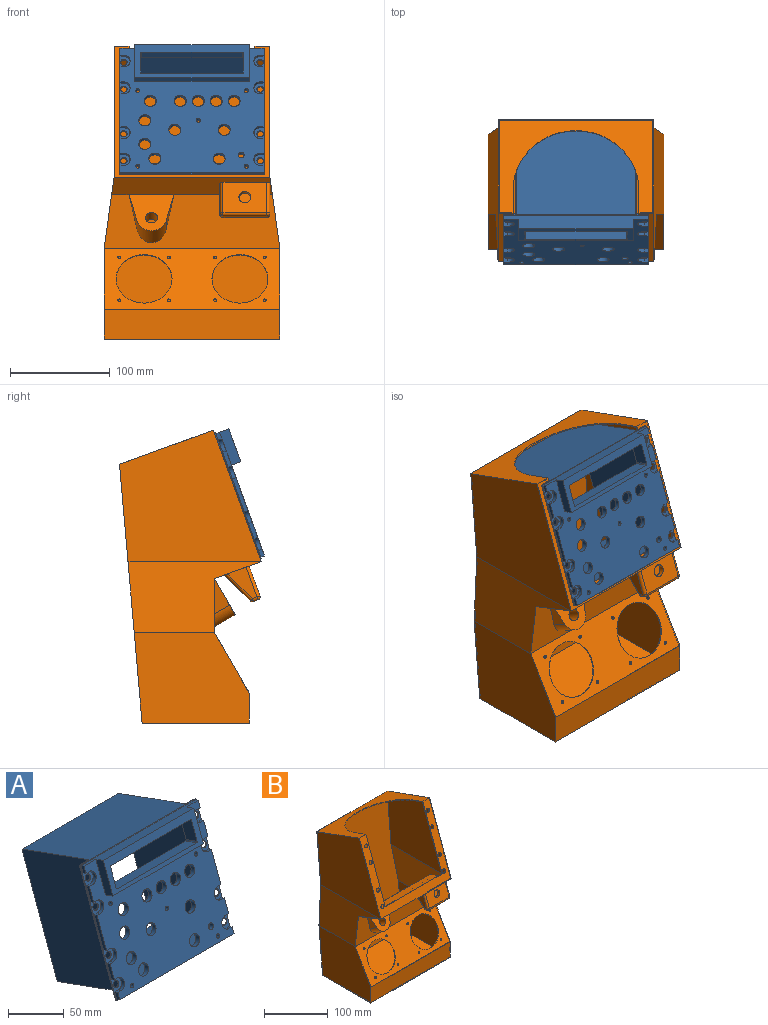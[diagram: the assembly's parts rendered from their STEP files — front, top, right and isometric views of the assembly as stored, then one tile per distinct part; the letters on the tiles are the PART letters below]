
ASSEMBLY  parts=2 mates=3
PART A: 89 faces, bbox 146x134.6x157.7 mm
  f0: plane 144.4x123.81mm, normal (0,-0.94,0.34), area 12776.2mm2, adj f8,f9,f10,f11,f12,f13,f14,f15
  f1: plane 120.61x120mm, normal (0,0.94,-0.34), area 11712.5mm2, adj f54,f55,f56,f57,f60,f61,f62,f63
  f2: plane 146x125.31mm, normal (0,0.94,-0.34), area 3302.6mm2, adj f4,f5,f6,f7,f44,f45,f46,f47
  f3: plane 146x125.31mm, normal (0,-0.94,0.34), area 1089.9mm2, adj f4,f5,f6,f7,f8,f9,f10,f11
  f4: plane 146x85.51mm, normal (0,0.34,0.94), area 11126mm2, adj f2,f3,f5,f7,f52,f53,f59
  f5: plane 125.65x46.55mm, normal (-1,0,0), area 133.4mm2, adj f2,f3,f4,f6
  f6: plane 146x0.94mm, normal (0,-0.34,-0.94), area 146mm2, adj f2,f3,f5,f7
  f7: plane 125.65x46.55mm, normal (1,0,0), area 133.4mm2, adj f2,f3,f4,f6
  f8: plane 8.08x6.2mm, normal (-1,0,0), area 28.6mm2, adj f0,f3,f9,f43
  f9: plane 144.4x3.76mm, normal (0,-0.34,-0.94), area 577.6mm2, adj f0,f3,f8,f10
  f10: plane 8.08x6.2mm, normal (1,0,0), area 28.6mm2, adj f0,f3,f9,f11
  f11: plane 3.96x3.76mm, normal (0,0.34,0.94), area 15.9mm2, adj f0,f3,f10,f12
  f12: cylinder r=6.35mm len=13.3mm, axis (0,0.94,-0.34), area 79.8mm2, adj f0,f3,f11,f13
  f13: plane 3.96x3.76mm, normal (0,-0.34,-0.94), area 15.9mm2, adj f0,f3,f12,f14
  f14: plane 16.29x9.19mm, normal (1,0,0), area 63.5mm2, adj f0,f3,f13,f15
  f15: plane 3.96x3.76mm, normal (0,0.34,0.94), area 15.9mm2, adj f0,f3,f14,f16
  f16: cylinder r=6.35mm len=13.3mm, axis (0,0.94,-0.34), area 79.8mm2, adj f0,f3,f15,f17
  f17: plane 3.96x3.76mm, normal (0,-0.34,-0.94), area 15.9mm2, adj f0,f3,f16,f18
  f18: plane 34.19x15.7mm, normal (1,0,0), area 139.7mm2, adj f0,f3,f17,f19
  f19: plane 3.96x3.76mm, normal (0,0.34,0.94), area 15.9mm2, adj f0,f3,f18,f20
  f20: cylinder r=6.35mm len=13.3mm, axis (0,0.94,-0.34), area 79.8mm2, adj f0,f3,f19,f21
  f21: plane 3.96x3.76mm, normal (0,-0.34,-0.94), area 15.9mm2, adj f0,f3,f20,f22
  f22: plane 16.29x9.19mm, normal (1,0,0), area 63.5mm2, adj f0,f3,f21,f23
  f23: plane 3.96x3.76mm, normal (0,0.34,0.94), area 15.9mm2, adj f0,f3,f22,f24
  f24: cylinder r=6.35mm len=13.3mm, axis (0,0.94,-0.34), area 79.8mm2, adj f0,f3,f23,f25
  f25: plane 3.96x3.76mm, normal (0,-0.34,-0.94), area 15.9mm2, adj f0,f3,f24,f26
  f26: plane 8.08x6.2mm, normal (1,0,0), area 28.6mm2, adj f0,f3,f25,f27
  f27: plane 144.4x13.16mm, normal (0,0.34,0.94), area 1721.6mm2, adj f0,f3,f26,f28,f77,f78,f80
  f28: plane 8.08x6.2mm, normal (-1,0,0), area 28.6mm2, adj f0,f3,f27,f29
  f29: plane 3.96x3.76mm, normal (0,-0.34,-0.94), area 15.9mm2, adj f0,f3,f28,f30
  f30: cylinder r=6.35mm len=13.3mm, axis (0,0.94,-0.34), area 79.8mm2, adj f0,f3,f29,f31
  f31: plane 3.96x3.76mm, normal (0,0.34,0.94), area 15.9mm2, adj f0,f3,f30,f32
  f32: plane 16.29x9.19mm, normal (-1,0,0), area 63.5mm2, adj f0,f3,f31,f33
  f33: plane 3.96x3.76mm, normal (0,-0.34,-0.94), area 15.9mm2, adj f0,f3,f32,f34
  f34: cylinder r=6.35mm len=13.3mm, axis (0,0.94,-0.34), area 79.8mm2, adj f0,f3,f33,f35
  f35: plane 3.96x3.76mm, normal (0,0.34,0.94), area 15.9mm2, adj f0,f3,f34,f36
  f36: plane 34.19x15.7mm, normal (-1,0,0), area 139.7mm2, adj f0,f3,f35,f37
  f37: plane 3.96x3.76mm, normal (0,-0.34,-0.94), area 15.9mm2, adj f0,f3,f36,f38
  f38: cylinder r=6.35mm len=13.3mm, axis (0,0.94,-0.34), area 79.8mm2, adj f0,f3,f37,f39
  f39: plane 3.96x3.76mm, normal (0,0.34,0.94), area 15.9mm2, adj f0,f3,f38,f40
  f40: plane 16.29x9.19mm, normal (-1,0,0), area 63.5mm2, adj f0,f3,f39,f41
  f41: plane 3.96x3.76mm, normal (0,-0.34,-0.94), area 15.9mm2, adj f0,f3,f40,f42
  f42: cylinder r=6.35mm len=13.3mm, axis (0,0.94,-0.34), area 79.8mm2, adj f0,f3,f41,f43
  f43: plane 3.96x3.76mm, normal (0,0.34,0.94), area 15.9mm2, adj f0,f3,f8,f42
  f44: cylinder r=3.24mm len=6.48mm, axis (0,-0.94,0.34), area 20.4mm2, adj f2,f3
  f45: cylinder r=3.24mm len=6.48mm, axis (0,-0.94,0.34), area 20.4mm2, adj f2,f3
  f46: cylinder r=3.24mm len=6.48mm, axis (0,-0.94,0.34), area 20.4mm2, adj f2,f3
  f47: cylinder r=3.24mm len=6.48mm, axis (0,-0.94,0.34), area 20.4mm2, adj f2,f3
  f48: cylinder r=3.24mm len=6.48mm, axis (0,-0.94,0.34), area 20.4mm2, adj f2,f3
  f49: cylinder r=3.24mm len=6.48mm, axis (0,-0.94,0.34), area 20.4mm2, adj f2,f3
  f50: cylinder r=3.24mm len=6.48mm, axis (0,-0.94,0.34), area 20.4mm2, adj f2,f3
  f51: cylinder r=3.24mm len=6.48mm, axis (0,-0.94,0.34), area 20.4mm2, adj f2,f3
  f52: plane 153.27x129.15mm, normal (-1,0,0), area 11731.5mm2, adj f2,f4,f58,f59
  f53: plane 153.27x129.15mm, normal (1,0,0), area 11731.5mm2, adj f2,f4,f58,f59
  f54: plane 120x84.57mm, normal (0,0.34,0.94), area 10800mm2, adj f1,f55,f57,f59
  f55: plane 151.39x128.47mm, normal (-1,0,0), area 11551.5mm2, adj f1,f54,f56,f59
  f56: plane 120x84.57mm, normal (0,-0.34,-0.94), area 10800mm2, adj f1,f55,f57,f59
  f57: plane 151.39x128.47mm, normal (1,0,0), area 11551.5mm2, adj f1,f54,f56,f59
  f58: plane 122x84.57mm, normal (0,-0.34,-0.94), area 10980mm2, adj f2,f52,f53,f59
  f59: plane 122.49x122mm, normal (0,0.94,-0.34), area 500.7mm2, adj f4,f52,f53,f54,f55,f56,f57,f58
  f60: cylinder r=2mm len=6.07mm, axis (0,-0.94,0.34), area 62.8mm2, adj f0,f1
  f61: cylinder r=6mm len=12.99mm, axis (0,-0.94,0.34), area 188.5mm2, adj f0,f1
  f62: cylinder r=6mm len=12.99mm, axis (0,-0.94,0.34), area 188.5mm2, adj f0,f1
  f63: cylinder r=6mm len=12.99mm, axis (0,-0.94,0.34), area 188.5mm2, adj f0,f1
  f64: cylinder r=6mm len=12.99mm, axis (0,-0.94,0.34), area 188.5mm2, adj f0,f1
  f65: cylinder r=2mm len=6.07mm, axis (0,-0.94,0.34), area 62.8mm2, adj f0,f1
  f66: cylinder r=3mm len=7.35mm, axis (0,-0.94,0.34), area 94.2mm2, adj f0,f1
  f67: cylinder r=6mm len=12.99mm, axis (0,-0.94,0.34), area 188.5mm2, adj f0,f1
  f68: cylinder r=6mm len=12.99mm, axis (0,-0.94,0.34), area 188.5mm2, adj f0,f1
  f69: cylinder r=2mm len=6.07mm, axis (0,-0.94,0.34), area 62.8mm2, adj f0,f1
  f70: cylinder r=2mm len=6.07mm, axis (0,-0.94,0.34), area 62.8mm2, adj f0,f1
  f71: cylinder r=2mm len=6.07mm, axis (0,-0.94,0.34), area 62.8mm2, adj f0,f1
  f72: cylinder r=6mm len=12.99mm, axis (0,-0.94,0.34), area 188.5mm2, adj f0,f1
  f73: cylinder r=6mm len=12.99mm, axis (0,-0.94,0.34), area 188.5mm2, adj f0,f1
  f74: cylinder r=6mm len=12.99mm, axis (0,-0.94,0.34), area 188.5mm2, adj f0,f1
  f75: cylinder r=6mm len=12.99mm, axis (0,-0.94,0.34), area 188.5mm2, adj f0,f1
  f76: cylinder r=6mm len=12.99mm, axis (0,-0.94,0.34), area 188.5mm2, adj f0,f1
  f77: plane 36.31x21.37mm, normal (1,0,0), area 350mm2, adj f0,f27,f79,f80
  f78: plane 36.31x21.37mm, normal (-1,0,0), area 350mm2, adj f0,f27,f79,f80
  f79: plane 114.4x9.4mm, normal (0,-0.34,-0.94), area 1144mm2, adj f0,f77,f78,f80
  f80: plane 114.4x32.89mm, normal (0,-0.94,0.34), area 1649.7mm2, adj f27,f77,f78,f79,f81,f82,f83,f84
  f81: cylinder r=1mm len=14.44mm, axis (0,-0.94,0.34), area 23.6mm2, adj f1,f80,f82,f88
  f82: plane 100.4x14.1mm, normal (0,0.34,0.94), area 1506mm2, adj f1,f80,f81,f83
  f83: cylinder r=1mm len=14.44mm, axis (0,-0.94,0.34), area 23.6mm2, adj f1,f80,f82,f84
  f84: plane 24.86x21.28mm, normal (-1,0,0), area 315mm2, adj f1,f80,f83,f85
  f85: cylinder r=1mm len=14.44mm, axis (0,-0.94,0.34), area 23.6mm2, adj f1,f80,f84,f86
  f86: plane 100.4x14.1mm, normal (0,-0.34,-0.94), area 1506mm2, adj f1,f80,f85,f87
  f87: cylinder r=1mm len=14.44mm, axis (0,-0.94,0.34), area 23.6mm2, adj f1,f80,f86,f88
  f88: plane 24.86x21.28mm, normal (1,0,0), area 315mm2, adj f1,f80,f81,f87
PART B: 74 faces, bbox 177.4x143.3x294.7 mm
  f0: plane 156x131.56mm, normal (0,-0.94,0.34), area 5826.2mm2, adj f1,f4,f9,f12,f15,f16,f17,f58
  f1: plane 156x93.97mm, normal (0,0.34,0.94), area 6215.5mm2, adj f0,f3,f9,f12,f15,f17,f31
  f2: plane 154x92.31mm, normal (0,-0.34,-0.94), area 5869.3mm2, adj f15,f17,f18,f19,f25,f28,f31
  f3: plane 259.01x175.97mm, normal (0,1,-0.09), area 43088.1mm2, adj f1,f8,f9,f10,f11,f12,f13,f14
  f4: plane 161.4x47.57mm, normal (0,-0.34,-0.94), area 6612.3mm2, adj f0,f5,f10,f13,f34,f35,f37,f38
  f5: plane 175.97x53.93mm, normal (0,-1,0), area 7499.9mm2, adj f4,f6,f10,f13,f51,f52,f53
  f6: plane 175.97x60.62mm, normal (0,-0.87,0.5), area 7335.1mm2, adj f5,f7,f11,f14,f32,f33,f66,f67
  f7: plane 175.97x30mm, normal (0,-1,0), area 5279mm2, adj f6,f8,f11,f14
  f8: plane 175.97x107.21mm, normal (0,0,-1), area 18864.8mm2, adj f3,f7,f11,f14
  f9: plane 141.85x131.56mm, normal (-1,0,0), area 13490.4mm2, adj f0,f1,f3,f10
  f10: plane 133.33x71.03mm, normal (-0.99,0,0.14), area 6376.9mm2, adj f3,f4,f5,f9,f11
  f11: plane 115.14x90.62mm, normal (-1,0,0), area 9013.6mm2, adj f3,f6,f7,f8,f10
  f12: plane 141.85x131.56mm, normal (1,0,0), area 13490.4mm2, adj f0,f1,f3,f13
  f13: plane 133.33x71.03mm, normal (0.99,0,0.14), area 6376.9mm2, adj f3,f4,f5,f12,f14
  f14: plane 115.14x90.62mm, normal (1,0,0), area 9013.6mm2, adj f3,f6,f7,f8,f13
  f15: plane 117.8x66.25mm, normal (1,0,0), area 149mm2, adj f0,f1,f2,f16,f18,f31
  f16: plane 126x0.94mm, normal (0,0.34,0.94), area 126mm2, adj f0,f15,f17,f18
  f17: plane 117.8x66.25mm, normal (-1,0,0), area 149mm2, adj f0,f1,f2,f16,f18,f31
  f18: plane 154x129.68mm, normal (0,0.94,-0.34), area 5364.2mm2, adj f2,f15,f16,f17,f20,f25,f28,f58
  f19: plane 257.33x173.97mm, normal (0,-1,0.09), area 42287.4mm2, adj f2,f24,f25,f26,f27,f28,f29,f30
  f20: plane 158.59x46.7mm, normal (0,0.34,0.94), area 7763.4mm2, adj f18,f21,f25,f26,f28,f29
  f21: plane 175.42x56.36mm, normal (0,1,0), area 8999.8mm2, adj f20,f22,f26,f27,f29,f30,f55
  f22: plane 173.97x60.62mm, normal (0,0.87,-0.5), area 7195.1mm2, adj f21,f23,f27,f30,f32,f33,f66,f67
  f23: plane 173.97x28.73mm, normal (0,1,0), area 4998.4mm2, adj f22,f24,f27,f30
  f24: plane 173.97x105.29mm, normal (0,0,1), area 18317mm2, adj f19,f23,f27,f30
  f25: plane 139.51x130.35mm, normal (1,0,0), area 13163.1mm2, adj f2,f18,f19,f20,f26
  f26: plane 129.21x71.03mm, normal (0.99,0,-0.14), area 6197mm2, adj f19,f20,f21,f25,f27
  f27: plane 113.13x89.55mm, normal (1,0,0), area 8712mm2, adj f19,f21,f22,f23,f24,f26
  f28: plane 139.51x130.35mm, normal (-1,0,0), area 13163.1mm2, adj f2,f18,f19,f20,f29
  f29: plane 129.21x71.03mm, normal (-0.99,0,-0.14), area 6197mm2, adj f19,f20,f21,f28,f30
  f30: plane 113.13x89.55mm, normal (-1,0,0), area 8712mm2, adj f19,f21,f22,f23,f24,f29
  f31: cylinder r=63mm len=126mm, axis (0,0.34,0.94), area 197.9mm2, adj f1,f2,f15,f17
  f32: cylinder r=28mm len=56mm, axis (0,-0.87,0.5), area 175.9mm2, adj f6,f22
  f33: cylinder r=28mm len=56mm, axis (0,-0.87,0.5), area 175.9mm2, adj f6,f22
  f34: plane 44x25.96mm, normal (0,0.71,-0.71), area 1615.1mm2, adj f4,f39,f40,f41
  f35: plane 44x30.07mm, normal (0,-0.94,0.34), area 1294.9mm2, adj f4,f45,f46,f50,f56
  f36: plane 44x4.78mm, normal (0,-0.34,-0.94), area 223.9mm2, adj f41,f44,f47,f50
  f37: plane 31.81x29.75mm, normal (-1,0,0), area 401.6mm2, adj f4,f39,f44,f45
  f38: plane 31.81x29.75mm, normal (1,0,0), area 401.6mm2, adj f4,f40,f46,f47
  f39: cylinder r=3mm len=28.08mm, axis (0,-0.71,-0.71), area 169.7mm2, adj f4,f34,f37,f42
  f40: cylinder r=3mm len=28.08mm, axis (0,0.71,0.71), area 169.7mm2, adj f4,f34,f38,f43
  f41: cylinder r=3mm len=44mm, axis (1,0,0), area 149.7mm2, adj f34,f36,f42,f43
  f42: sphere r=3mm, area 10.2mm2, adj f39,f41,f44
  f43: sphere r=3mm, area 10.2mm2, adj f40,f41,f47
  f44: cylinder r=3mm len=5.81mm, axis (0,-0.94,0.34), area 24mm2, adj f36,f37,f42,f48
  f45: cylinder r=3mm len=31.1mm, axis (0,0.34,0.94), area 150.8mm2, adj f4,f35,f37,f48
  f46: cylinder r=3mm len=31.1mm, axis (0,-0.34,-0.94), area 150.8mm2, adj f4,f35,f38,f49
  f47: cylinder r=3mm len=5.81mm, axis (0,0.94,-0.34), area 24mm2, adj f36,f38,f43,f49
  f48: sphere r=3mm, area 13.4mm2, adj f44,f45,f50
  f49: sphere r=3mm, area 13.4mm2, adj f46,f47,f50
  f50: cylinder r=3mm len=44mm, axis (1,0,0), area 207.3mm2, adj f35,f36,f48,f49
  f51: plane 35.23x15.25mm, normal (0.97,-0.13,-0.22), area 277.7mm2, adj f5,f53,f54
  f52: plane 35.23x15.25mm, normal (-0.97,-0.13,-0.22), area 277.7mm2, adj f5,f53,f54
  f53: cylinder r=15mm len=29.02mm, axis (0,-0.87,0.5), area 859.5mm2, adj f5,f51,f52,f54
  f54: plane 45x36.12mm, normal (0,-0.87,0.5), area 1256.7mm2, adj f4,f51,f52,f53,f55
  f55: cylinder r=6mm len=23.37mm, axis (0,-0.87,0.5), area 629.3mm2, adj f21,f54
  f56: cylinder r=6mm len=12.99mm, axis (0,-0.94,0.34), area 188.5mm2, adj f35,f57
  f57: plane 12x11.28mm, normal (0,-0.94,0.34), area 113.1mm2, adj f56
  f58: cylinder r=3.24mm len=6.48mm, axis (0,-0.94,0.34), area 20.4mm2, adj f0,f18
  f59: cylinder r=3.24mm len=6.48mm, axis (0,-0.94,0.34), area 20.4mm2, adj f0,f18
  f60: cylinder r=3.24mm len=6.48mm, axis (0,-0.94,0.34), area 20.4mm2, adj f0,f18
  f61: cylinder r=3.24mm len=6.48mm, axis (0,-0.94,0.34), area 20.4mm2, adj f0,f18
  f62: cylinder r=3.24mm len=6.48mm, axis (0,-0.94,0.34), area 20.4mm2, adj f0,f18
  f63: cylinder r=3.24mm len=6.48mm, axis (0,-0.94,0.34), area 20.4mm2, adj f0,f18
  f64: cylinder r=3.24mm len=6.48mm, axis (0,-0.94,0.34), area 20.4mm2, adj f0,f18
  f65: cylinder r=3.24mm len=6.48mm, axis (0,-0.94,0.34), area 20.4mm2, adj f0,f18
  f66: cylinder r=1.5mm len=3.1mm, axis (0,-0.87,0.5), area 9.4mm2, adj f6,f22
  f67: cylinder r=1.5mm len=3.1mm, axis (0,-0.87,0.5), area 9.4mm2, adj f6,f22
  f68: cylinder r=1.5mm len=3.1mm, axis (0,-0.87,0.5), area 9.4mm2, adj f6,f22
  f69: cylinder r=1.5mm len=3.1mm, axis (0,-0.87,0.5), area 9.4mm2, adj f6,f22
  f70: cylinder r=1.5mm len=3.1mm, axis (0,-0.87,0.5), area 9.4mm2, adj f6,f22
  f71: cylinder r=1.5mm len=3.1mm, axis (0,-0.87,0.5), area 9.4mm2, adj f6,f22
  f72: cylinder r=1.5mm len=3.1mm, axis (0,-0.87,0.5), area 9.4mm2, adj f6,f22
  f73: cylinder r=1.5mm len=3.1mm, axis (0,-0.87,0.5), area 9.4mm2, adj f6,f22
PLACE A t=(-98.48,-94.61,50.93)mm
PLACE B t=(-98.48,-94.61,50.93)mm fixed
MATE revolute A.f24 <-> B.f65  axis (0,0.94,-0.34) through (69.76,-100.63,34.38)mm
MATE revolute A.f30 <-> B.f58  axis (0,0.94,-0.34) through (-66.71,-100.63,34.38)mm
MATE planar A.f1 <-> B.f0  axis (0,0.94,-0.34) through (1.52,-121.02,-21.64)mm
